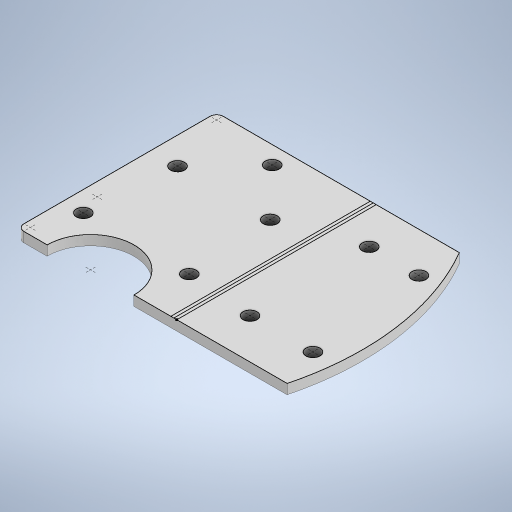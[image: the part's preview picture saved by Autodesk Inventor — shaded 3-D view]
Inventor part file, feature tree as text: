
AUTODESK INVENTOR PART (.ipt)
format: ipt  version: 2024.2 (Build 282272000, 272)  size: 278,528 bytes
history: native  units: in
note: dims shown in document units (in); Inventor stores cm internally (conversion verified against a paired STEP export)
features: sketch x1, extrude x1
ambient origin geometry x8: Origin, YZ Plane, XZ Plane, XY Plane, X Axis, Y Axis, Z Axis, Center Point
bodies: Solid1 (feature_tree)
feature tree (2):
  sketch  "Sketch1"  dims[d1=0.0591in d2=0.0in]
  extrude  "Extrusion1"  [1 undecoded]
note: 1 required parameter value undecoded (feature->parameter linkage not recoverable at this tier; creation-order binding heuristic only, values carry confidence <= 0.55)
